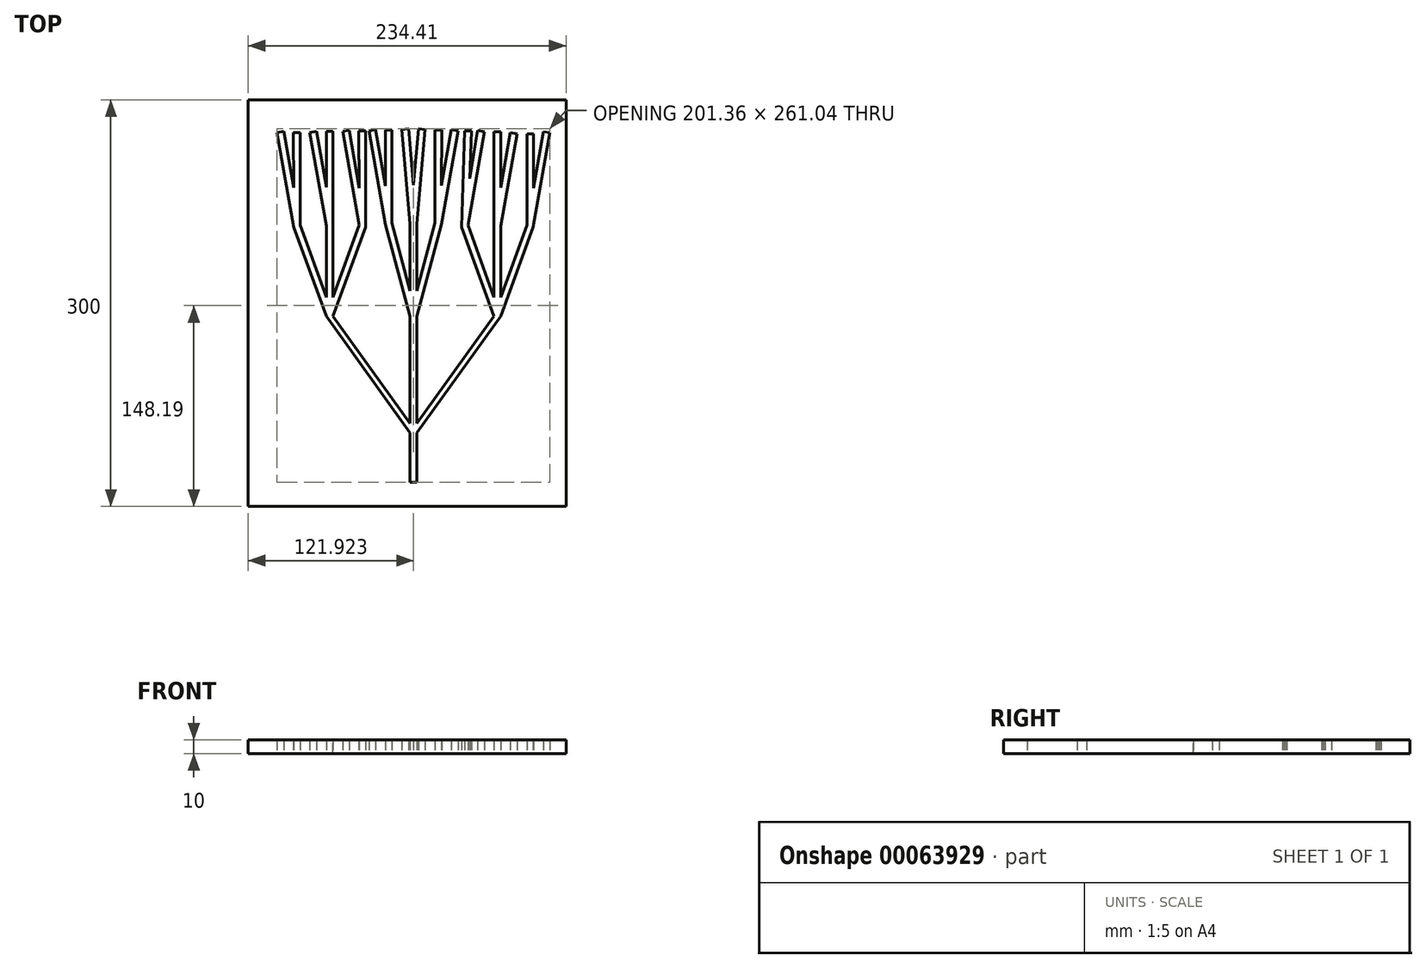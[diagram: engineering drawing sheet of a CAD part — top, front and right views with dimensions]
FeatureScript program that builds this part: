
annotation { "Feature Type Name" : "Feature", "Feature Type Description" : "" }
export const myFeature = defineFeature(function(context is Context, id is Id, definition is map)
    precondition{}
    {
        {
            var Q0;
            Q0=qCreatedBy(makeId("Top.planeOp"),FACE);
            var sketch = newSketch(context, id + "F0", { "sketchPlane" : qUnion([Q0])});
            skLineSegment(sketch, "E0", {"start": v(0, -654.78) * mm, "end": v(25, -654.78) * mm});
            skLineSegment(sketch, "E1", {"start": v(25, -672.12) * mm, "end": v(-25.43, -672.12) * mm});
            skPoint(sketch, "E2.endSnap0", {"position": v(23.1, -65.35) * mm});
            skLineSegment(sketch, "E3", {"start": v(20.6, -29.43) * mm, "end": v(2.48, 38.18) * mm});
            skLineSegment(sketch, "E4", {"start": v(7.31, 39.48) * mm, "end": v(25.6, -29.43) * mm});
            skLineSegment(sketch, "E5", {"start": v(20.6, -29.43) * mm, "end": v(20.6, 38.83) * mm});
            skLineSegment(sketch, "E6", {"start": v(25.6, -29.43) * mm, "end": v(25.6, 38.83) * mm});
            skLineSegment(sketch, "E7", {"start": v(25.6, -29.43) * mm, "end": v(43.72, 38.18) * mm});
            skLineSegment(sketch, "E8", {"start": v(38.89, 39.48) * mm, "end": v(20.6, -29.43) * mm});
            skLineSegment(sketch, "E9", {"start": v(-41.25, -29.43) * mm, "end": v(-65.19, 36.35) * mm});
            skLineSegment(sketch, "E10", {"start": v(-60.49, 38.06) * mm, "end": v(-36.25, -29.43) * mm});
            skLineSegment(sketch, "E11", {"start": v(-36.25, -29.43) * mm, "end": v(-12.3, 36.35) * mm});
            skLineSegment(sketch, "E12", {"start": v(-36.25, -29.43) * mm, "end": v(-36.25, 37.2) * mm});
            skLineSegment(sketch, "E13", {"start": v(-41.25, 37.2) * mm, "end": v(-41.25, -29.43) * mm});
            skLineSegment(sketch, "E14", {"start": v(82.47, -29.49) * mm, "end": v(58.53, 36.29) * mm});
            skLineSegment(sketch, "E15", {"start": v(63.23, 38) * mm, "end": v(87.47, -29.49) * mm});
            skLineSegment(sketch, "E16", {"start": v(106.72, 38) * mm, "end": v(82.47, -29.49) * mm});
            skLineSegment(sketch, "E17", {"start": v(87.47, -29.49) * mm, "end": v(111.41, 36.29) * mm});
            skLineSegment(sketch, "E18", {"start": v(87.47, -29.49) * mm, "end": v(87.47, 37.14) * mm});
            skLineSegment(sketch, "E19", {"start": v(82.47, 37.14) * mm, "end": v(82.47, -29.49) * mm});
            skLineSegment(sketch, "E20", {"start": v(-17, 38.06) * mm, "end": v(-41.25, -29.43) * mm});
            skLineSegment(sketch, "E21", {"start": v(20.6, 38.83) * mm, "end": v(14.5, 108.56) * mm});
            skLineSegment(sketch, "E22", {"start": v(25.6, 38.83) * mm, "end": v(31.7, 108.56) * mm});
            skLineSegment(sketch, "E23", {"start": v(14.5, 108.56) * mm, "end": v(19.48, 109) * mm});
            skLineSegment(sketch, "E24", {"start": v(31.7, 108.56) * mm, "end": v(26.72, 109) * mm});
            skLineSegment(sketch, "E25", {"start": v(26.72, 109) * mm, "end": v(20.6, 38.83) * mm});
            skLineSegment(sketch, "E26", {"start": v(19.48, 109) * mm, "end": v(25.6, 38.83) * mm});
            skLineSegment(sketch, "E27", {"start": v(7.31, 39.48) * mm, "end": v(7.31, 108.09) * mm});
            skLineSegment(sketch, "E28", {"start": v(2.48, 108.09) * mm, "end": v(2.48, 38.18) * mm});
            skLineSegment(sketch, "E29", {"start": v(2.48, 108.09) * mm, "end": v(7.31, 108.09) * mm});
            skLineSegment(sketch, "E30", {"start": v(7.31, 39.48) * mm, "end": v(-4.84, 108.41) * mm});
            skLineSegment(sketch, "E31", {"start": v(-4.84, 108.41) * mm, "end": v(-9.77, 107.54) * mm});
            skLineSegment(sketch, "E32", {"start": v(-9.77, 107.54) * mm, "end": v(2.48, 38.18) * mm});
            skLineSegment(sketch, "E33", {"start": v(38.89, 39.48) * mm, "end": v(38.89, 108.09) * mm});
            skLineSegment(sketch, "E34", {"start": v(38.89, 108.09) * mm, "end": v(43.89, 108.09) * mm});
            skLineSegment(sketch, "E35", {"start": v(43.89, 108.09) * mm, "end": v(43.72, 38.18) * mm});
            skLineSegment(sketch, "E36", {"start": v(38.89, 39.48) * mm, "end": v(51.04, 108.41) * mm});
            skLineSegment(sketch, "E37", {"start": v(51.04, 108.41) * mm, "end": v(55.97, 107.54) * mm});
            skLineSegment(sketch, "E38", {"start": v(55.97, 107.54) * mm, "end": v(43.72, 38.18) * mm});
            skLineSegment(sketch, "E39", {"start": v(58.53, 36.29) * mm, "end": v(60.88, 107.54) * mm});
            skLineSegment(sketch, "E40", {"start": v(60.88, 107.54) * mm, "end": v(65.88, 107.38) * mm});
            skLineSegment(sketch, "E41", {"start": v(65.88, 107.38) * mm, "end": v(63.23, 38) * mm});
            skLineSegment(sketch, "E42", {"start": v(-12.3, 36.35) * mm, "end": v(-12.3, 107.54) * mm});
            skLineSegment(sketch, "E43", {"start": v(-12.3, 107.54) * mm, "end": v(-17.3, 107.54) * mm});
            skLineSegment(sketch, "E44", {"start": v(-17.3, 107.54) * mm, "end": v(-17, 38.06) * mm});
            skLineSegment(sketch, "E45", {"start": v(-17, 38.06) * mm, "end": v(-29.16, 107) * mm});
            skLineSegment(sketch, "E46", {"start": v(-29.16, 107) * mm, "end": v(-24.23, 107.86) * mm});
            skLineSegment(sketch, "E47", {"start": v(-24.23, 107.86) * mm, "end": v(-12.3, 36.35) * mm});
            skLineSegment(sketch, "E48", {"start": v(63.23, 38) * mm, "end": v(75.38, 106.94) * mm});
            skLineSegment(sketch, "E49", {"start": v(75.38, 106.94) * mm, "end": v(70.46, 107.8) * mm});
            skLineSegment(sketch, "E50", {"start": v(70.46, 107.8) * mm, "end": v(58.53, 36.29) * mm});
            skLineSegment(sketch, "E51", {"start": v(82.47, 37.14) * mm, "end": v(82.47, 106.94) * mm});
            skLineSegment(sketch, "E52", {"start": v(82.47, 106.94) * mm, "end": v(87.47, 106.94) * mm});
            skLineSegment(sketch, "E53", {"start": v(87.47, 106.94) * mm, "end": v(87.47, 37.14) * mm});
            skLineSegment(sketch, "E54", {"start": v(82.47, 37.14) * mm, "end": v(94.63, 106.08) * mm});
            skLineSegment(sketch, "E55", {"start": v(94.63, 106.08) * mm, "end": v(99.55, 105.21) * mm});
            skLineSegment(sketch, "E56", {"start": v(99.55, 105.21) * mm, "end": v(87.47, 37.14) * mm});
            skLineSegment(sketch, "E57", {"start": v(-36.25, 37.2) * mm, "end": v(-36.25, 107) * mm});
            skLineSegment(sketch, "E58", {"start": v(-41.25, 37.2) * mm, "end": v(-41.25, 107) * mm});
            skLineSegment(sketch, "E59", {"start": v(-41.25, 107) * mm, "end": v(-36.25, 107) * mm});
            skLineSegment(sketch, "E60", {"start": v(-41.25, 37.2) * mm, "end": v(-53.4, 106.14) * mm});
            skLineSegment(sketch, "E61", {"start": v(-53.4, 106.14) * mm, "end": v(-48.48, 107) * mm});
            skLineSegment(sketch, "E62", {"start": v(-48.48, 107) * mm, "end": v(-36.25, 37.2) * mm});
            skLineSegment(sketch, "E63", {"start": v(-60.49, 38.06) * mm, "end": v(-60.49, 106.14) * mm});
            skLineSegment(sketch, "E64", {"start": v(-60.49, 106.14) * mm, "end": v(-65.49, 106.14) * mm});
            skLineSegment(sketch, "E65", {"start": v(-65.49, 106.14) * mm, "end": v(-65.19, 36.35) * mm});
            skLineSegment(sketch, "E66", {"start": v(-60.49, 38.06) * mm, "end": v(-72.64, 107) * mm});
            skLineSegment(sketch, "E67", {"start": v(-72.64, 107) * mm, "end": v(-77.57, 106.13) * mm});
            skLineSegment(sketch, "E68", {"start": v(-77.57, 106.13) * mm, "end": v(-65.19, 36.35) * mm});
            skLineSegment(sketch, "E69", {"start": v(106.72, 38) * mm, "end": v(106.72, 105.21) * mm});
            skLineSegment(sketch, "E70", {"start": v(106.72, 105.21) * mm, "end": v(111.72, 105.21) * mm});
            skLineSegment(sketch, "E71", {"start": v(111.72, 105.21) * mm, "end": v(111.41, 36.29) * mm});
            skLineSegment(sketch, "E72", {"start": v(106.72, 38) * mm, "end": v(118.87, 106.94) * mm});
            skLineSegment(sketch, "E73", {"start": v(118.87, 106.94) * mm, "end": v(123.8, 106.07) * mm});
            skLineSegment(sketch, "E74", {"start": v(123.8, 106.07) * mm, "end": v(111.41, 36.29) * mm});
            skLineSegment(sketch, "E75", {"start": v(20.6, -29.43) * mm, "end": v(20.6, -115.3) * mm});
            skLineSegment(sketch, "E76", {"start": v(25.6, -29.43) * mm, "end": v(25.6, -115.3) * mm});
            skLineSegment(sketch, "E77", {"start": v(25.6, -115.3) * mm, "end": v(87.47, -29.49) * mm});
            skLineSegment(sketch, "E78", {"start": v(82.47, -29.49) * mm, "end": v(20.6, -115.3) * mm});
            skLineSegment(sketch, "E79", {"start": v(20.6, -115.3) * mm, "end": v(-41.25, -29.43) * mm});
            skLineSegment(sketch, "E80", {"start": v(-36.25, -29.43) * mm, "end": v(25.6, -115.3) * mm});
            skLineSegment(sketch, "E81", {"start": v(135.6, 130.3) * mm, "end": v(23.1, 130.3) * mm});
            skLineSegment(sketch, "E82", {"start": v(23.1, 130.3) * mm, "end": v(-98.81, 130.3) * mm});
            skLineSegment(sketch, "E83", {"start": v(-98.81, -169.7) * mm, "end": v(135.6, -169.7) * mm});
            skLineSegment(sketch, "E84", {"start": v(135.6, -169.7) * mm, "end": v(135.6, 130.3) * mm});
            skLineSegment(sketch, "E85", {"start": v(-98.81, -169.7) * mm, "end": v(-98.81, 130.3) * mm});
            skLineSegment(sketch, "E86", {"start": v(20.6, -115.3) * mm, "end": v(20.6, -152.04) * mm});
            skLineSegment(sketch, "E87", {"start": v(20.6, -152.04) * mm, "end": v(25.6, -152.04) * mm});
            skLineSegment(sketch, "E88", {"start": v(25.6, -152.04) * mm, "end": v(25.6, -115.3) * mm});
            skSolve(sketch);
        }
        {
            var Q0;
            {var subQ46=sQuery(id+"F0.wireOp",EDGE,"E3");Q0=makeQuery(id+"F0.imprint","IMPRINT",FACE,{"disambiguationData":[TD([[makeQuery(id+"F0.imprint","IMPRINT",EDGE,{"derivedFrom":subQ46}),1.0]])]});}
            extrude(context, id + "F1", {"entities" : qUnion([Q0]), "depth" : 10 * mm});
        }
    });
